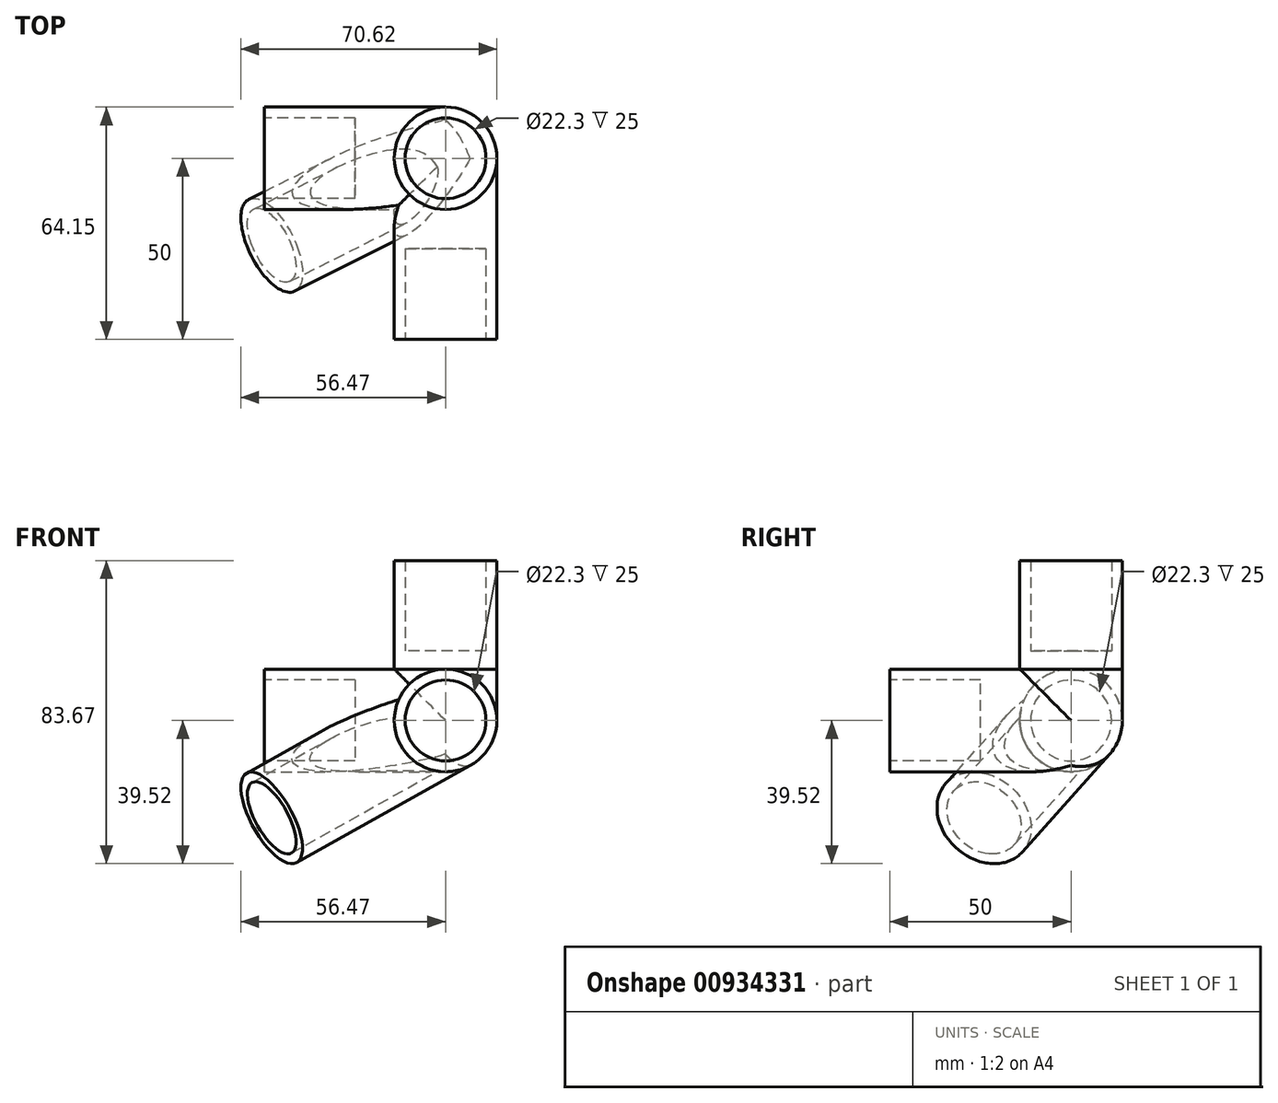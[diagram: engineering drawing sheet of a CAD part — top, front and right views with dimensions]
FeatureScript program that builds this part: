
annotation { "Feature Type Name" : "Feature", "Feature Type Description" : "" }
export const myFeature = defineFeature(function(context is Context, id is Id, definition is map)
    precondition{}
    {
        {
            var Q0;
            Q0=qCreatedBy(makeId("Top.planeOp"),FACE);
            var sketch = newSketch(context, id + "F0", { "sketchPlane" : qUnion([Q0])});
            skCircle(sketch, "E0", {"center": v(0, 0) * mm, "radius": 11.15 * mm});
            skCircle(sketch, "E1", {"center": v(0, 0) * mm, "radius": 14.15 * mm});
            skSolve(sketch);
        }
        {
            var Q0;
            Q0=qSketchRegion(id+"F0",true);
            extrude(context, id + "F1", {"entities" : qUnion([Q0]), "depth" : 25 * mm, "offsetDistance" : 25 * mm});
        }
        {
            var Q0;
            Q0=qCreatedBy(makeId("Top.planeOp"),FACE);
            var sketch = newSketch(context, id + "F2", { "sketchPlane" : qUnion([Q0])});
            skCircle(sketch, "E2", {"center": v(0, 0) * mm, "radius": 14.15 * mm});
            skSolve(sketch);
        }
        {
            var Q0;
            Q0=qSketchRegion(id+"F2",true);
            extrude(context, id + "F3", {"entities" : qUnion([Q0]), "operationType" : NewBodyOperationType.ADD, "oppositeDirection" : true, "depth" : 5 * mm, "offsetDistance" : 25 * mm});
        }
        {
            var Q0;
            Q0=qCreatedBy(makeId("Right.planeOp"),FACE);
            var sketch = newSketch(context, id + "F4", { "sketchPlane" : qUnion([Q0])});
            skLineSegment(sketch, "E3", {"start": v(0, 0) * mm, "end": v(0, -5) * mm, "construction": true});
            skLineSegment(sketch, "E4", {"start": v(0, -5) * mm, "end": v(0, -19.15) * mm, "construction": true});
            skCircle(sketch, "E5", {"center": v(0, -19.15) * mm, "radius": 14.15 * mm});
            skCircle(sketch, "E6", {"center": v(0, -19.15) * mm, "radius": 11.15 * mm});
            skSolve(sketch);
        }
        {
            var Q0;
            Q0=qSketchRegion(id+"F4",true);
            extrude(context, id + "F5", {"entities" : qUnion([Q0]), "operationType" : NewBodyOperationType.ADD, "oppositeDirection" : true, "depth" : 50 * mm, "offsetDistance" : 25 * mm});
        }
        {
            var Q0;
            Q0=qCreatedBy(makeId("Front.planeOp"),FACE);
            var sketch = newSketch(context, id + "F6", { "sketchPlane" : qUnion([Q0])});
            skLineSegment(sketch, "E7", {"start": v(0, 0) * mm, "end": v(0, -5) * mm, "construction": true});
            skLineSegment(sketch, "E8", {"start": v(0, -5) * mm, "end": v(0, -19.15) * mm, "construction": true});
            skCircle(sketch, "E9", {"center": v(0, -19.15) * mm, "radius": 14.15 * mm});
            skCircle(sketch, "E10", {"center": v(0, -19.15) * mm, "radius": 11.15 * mm});
            skSolve(sketch);
        }
        {
            var Q0;
            Q0=qSketchRegion(id+"F6",true);
            extrude(context, id + "F7", {"entities" : qUnion([Q0]), "operationType" : NewBodyOperationType.ADD, "depth" : 50 * mm, "offsetDistance" : 25 * mm});
        }
        {
            var Q0;
            {var subQ0=sQuery(id+"F4.wireOp",EDGE,"E6");var subQ1=sQuery(id+"F4.wireOp",EDGE,"E5");var subQ2=sQuery(id+"F6.wireOp",EDGE,"E10");var subQ3=sQuery(id+"F6.wireOp",EDGE,"E9");var subQ4=makeQuery(id+"F7.opExtrude","CAP_FACE",FACE,{"disambiguationData":[OSD([subQ3,subQ2])],"isStart":true});Q0=makeQuery(id+"F7.boolean.opBoolean","SPLIT",FACE,{"disambiguationData":[TD([makeQuery(id+"F5.opExtrude","SWEPT_FACE",FACE,{"disambiguationData":[OSD([subQ1])]}),makeQuery(id+"F5.opExtrude","CAP_FACE",FACE,{"disambiguationData":[OSD([subQ1,subQ0])],"isStart":true}),makeQuery(id+"F5.opExtrude","SWEPT_FACE",FACE,{"disambiguationData":[OSD([subQ0])]}),makeQuery(id+"F7.opExtrude","SWEPT_FACE",FACE,{"disambiguationData":[OSD([subQ3])]}),subQ4,makeQuery(id+"F7.opExtrude","SWEPT_FACE",FACE,{"disambiguationData":[OSD([subQ2])]})])],"derivedFrom":subQ4});}
            var sketch = newSketch(context, id + "F8", { "sketchPlane" : qUnion([Q0])});
            skArc(sketch, "E11", {"start": v(-14.15, -19.15) * mm, "mid": v(-10, -29.16) * mm, "end": v(0, -33.3) * mm});
            skLineSegment(sketch, "E12", {"start": v(0, -5) * mm, "end": v(-14.15, -5) * mm});
            skLineSegment(sketch, "E13", {"start": v(-14.15, -19.15) * mm, "end": v(-14.15, -5) * mm});
            skLineSegment(sketch, "E14", {"start": v(0, -33.3) * mm, "end": v(0, -5) * mm});
            skSolve(sketch);
        }
        {
            var Q0;
            Q0=qSketchRegion(id+"F8",true);
            var Q1;
            Q1=sQuery(id+"F8.wireOp",EDGE,"E14");
            revolve(context, id + "F9", {"surfaceOperationType" : NewSurfaceOperationType.NEW, "entities" : qUnion([Q0]), "axis" : qUnion([Q1]), "revolveType" : RevolveType.ONE_DIRECTION, "angle" : 360 * degree});
        }
        {
            var Q0;
            Q0=makeQuery(id+"F5.opExtrude","CAP_FACE",FACE,{"disambiguationData":[OSD([sQuery(id+"F4.wireOp",EDGE,"E5"),sQuery(id+"F4.wireOp",EDGE,"E6")])],"isStart":false});
            var sketch = newSketch(context, id + "F10", { "sketchPlane" : qUnion([Q0])});
            skLineSegment(sketch, "E15", {"start": v(0, 0) * mm, "end": v(0, -33.3) * mm, "construction": true});
            skPoint(sketch, "E16.center.orphan", {"position": v(0, -19.15) * mm});
            skCircle(sketch, "E17", {"center": v(0, -19.15) * mm, "radius": 11.15 * mm});
            skSolve(sketch);
        }
        {
            var Q0;
            Q0=makeQuery(id+"F7.opExtrude","CAP_FACE",FACE,{"disambiguationData":[OSD([sQuery(id+"F6.wireOp",EDGE,"E9"),sQuery(id+"F6.wireOp",EDGE,"E10")])],"isStart":false});
            var sketch = newSketch(context, id + "F11", { "sketchPlane" : qUnion([Q0])});
            skCircle(sketch, "E18", {"center": v(0, -19.15) * mm, "radius": 11.15 * mm});
            skSolve(sketch);
        }
        {
            var Q0;
            Q0=qCreatedBy(makeId("Right.planeOp"),FACE);
            var sketch = newSketch(context, id + "F12", { "sketchPlane" : qUnion([Q0])});
            skLineSegment(sketch, "E19", {"start": v(0, 43.35) * mm, "end": v(0, -51.42) * mm, "construction": true});
            skSolve(sketch);
        }
        {
            var Q0;
            Q0=sQuery(id+"F12.wireOp",EDGE,"E19");
            var Q1;
            Q1=qCreatedBy(makeId("Front.planeOp"),FACE);
            cPlane(context, id + "F13", {"entities" : qUnion([Q0, Q1]), "cplaneType" : CPlaneType.LINE_ANGLE, "offset" : 25 * mm, "angle" : 26.6 * degree, "oppositeDirection" : true, "width" : 150 * mm, "height" : 150 * mm});
        }
        {
            var Q0;
            Q0=qCreatedBy(id+"F13.planeOp",FACE);
            var sketch = newSketch(context, id + "F14", { "sketchPlane" : qUnion([Q0])});
            skLineSegment(sketch, "E20", {"start": v(0, 0) * mm, "end": v(0, -19.15) * mm, "construction": true});
            skLineSegment(sketch, "E21", {"start": v(0, -33.3) * mm, "end": v(0, -19.15) * mm, "construction": true});
            skLineSegment(sketch, "E22", {"start": v(0, -19.15) * mm, "end": v(26.82, -32.58) * mm, "construction": true});
            skLineSegment(sketch, "E23", {"start": v(0, -19.15) * mm, "end": v(69.41, -19.15) * mm, "construction": true});
            skSolve(sketch);
        }
        {
            var Q0;
            Q0=sQuery(id+"F14.wireOp",VERTEX,"E22.end");
            var Q1;
            Q1=sQuery(id+"F14.wireOp",EDGE,"E22");
            cPlane(context, id + "F15", {"entities" : qUnion([Q0, Q1]), "cplaneType" : CPlaneType.LINE_POINT, "offset" : 25 * mm, "width" : 150 * mm, "height" : 150 * mm});
        }
        {
            var Q0;
            Q0=qCreatedBy(id+"F15.planeOp",FACE);
            var sketch = newSketch(context, id + "F16", { "sketchPlane" : qUnion([Q0])});
            skCircle(sketch, "E24", {"center": v(-3.75, -16.7) * mm, "radius": 14.15 * mm});
            skCircle(sketch, "E25", {"center": v(-3.75, -16.7) * mm, "radius": 11.15 * mm});
            skSolve(sketch);
        }
        {
            var Q0;
            Q0=qSketchRegion(id+"F16",true);
            extrude(context, id + "F17", {"entities" : qUnion([Q0]), "operationType" : NewBodyOperationType.ADD, "endBound" : BoundingType.SYMMETRIC, "depth" : 60 * mm, "offsetDistance" : 25 * mm});
        }
        {
            var Q0;
            Q0=qSketchRegion(id+"F10",true);
            extrude(context, id + "F18", {"entities" : qUnion([Q0]), "operationType" : NewBodyOperationType.REMOVE, "oppositeDirection" : true, "depth" : 35 * mm, "offsetDistance" : 25 * mm});
        }
        {
            var Q0;
            Q0=qSketchRegion(id+"F11",true);
            extrude(context, id + "F19", {"entities" : qUnion([Q0]), "operationType" : NewBodyOperationType.REMOVE, "oppositeDirection" : true, "depth" : 30 * mm, "offsetDistance" : 25 * mm});
        }
        {
            var Q0;
            Q0=makeQuery(id+"F5.opExtrude","CAP_FACE",FACE,{"disambiguationData":[OSD([sQuery(id+"F4.wireOp",EDGE,"E5"),sQuery(id+"F4.wireOp",EDGE,"E6")])],"isStart":false});
            var sketch = newSketch(context, id + "F20", { "sketchPlane" : qUnion([Q0])});
            skCircle(sketch, "E26", {"center": v(0, -19.15) * mm, "radius": 11.15 * mm});
            skSolve(sketch);
        }
        {
            var Q0;
            Q0=qSketchRegion(id+"F20",true);
            extrude(context, id + "F21", {"entities" : qUnion([Q0]), "operationType" : NewBodyOperationType.ADD, "oppositeDirection" : true, "depth" : 50 * mm, "offsetDistance" : 25 * mm});
        }
        {
            var Q0;
            Q0=makeQuery(id+"F21.boolean.opBoolean","MERGE",FACE,{"derivedFrom":[makeQuery(id+"F5.opExtrude","CAP_FACE",FACE,{"disambiguationData":[OSD([sQuery(id+"F4.wireOp",EDGE,"E5"),sQuery(id+"F4.wireOp",EDGE,"E6")])],"isStart":false}),makeQuery(id+"F21.opExtrude","CAP_FACE",FACE,{"disambiguationData":[OSD([sQuery(id+"F20.wireOp",EDGE,"E26")])],"isStart":true})]});
            var sketch = newSketch(context, id + "F22", { "sketchPlane" : qUnion([Q0])});
            skCircle(sketch, "E27", {"center": v(0, -19.15) * mm, "radius": 11.15 * mm});
            skSolve(sketch);
        }
        {
            var Q0;
            Q0=qSketchRegion(id+"F22",true);
            extrude(context, id + "F23", {"entities" : qUnion([Q0]), "operationType" : NewBodyOperationType.REMOVE, "oppositeDirection" : true, "depth" : 25 * mm, "offsetDistance" : 25 * mm});
        }
        {
            var Q0;
            Q0=makeQuery(id+"F7.opExtrude","CAP_FACE",FACE,{"disambiguationData":[OSD([sQuery(id+"F6.wireOp",EDGE,"E9"),sQuery(id+"F6.wireOp",EDGE,"E10")])],"isStart":false});
            var sketch = newSketch(context, id + "F24", { "sketchPlane" : qUnion([Q0])});
            skCircle(sketch, "E28", {"center": v(0, -19.15) * mm, "radius": 11.15 * mm});
            skSolve(sketch);
        }
        {
            var Q0;
            Q0=qSketchRegion(id+"F24",true);
            extrude(context, id + "F25", {"entities" : qUnion([Q0]), "operationType" : NewBodyOperationType.ADD, "oppositeDirection" : true, "depth" : 50.1 * mm, "offsetDistance" : 25 * mm});
        }
        {
            var Q0;
            Q0=makeQuery(id+"F25.boolean.opBoolean","MERGE",FACE,{"derivedFrom":[makeQuery(id+"F7.opExtrude","CAP_FACE",FACE,{"disambiguationData":[OSD([sQuery(id+"F6.wireOp",EDGE,"E9"),sQuery(id+"F6.wireOp",EDGE,"E10")])],"isStart":false}),makeQuery(id+"F25.opExtrude","CAP_FACE",FACE,{"disambiguationData":[OSD([sQuery(id+"F24.wireOp",EDGE,"E28")])],"isStart":true})]});
            var sketch = newSketch(context, id + "F26", { "sketchPlane" : qUnion([Q0])});
            skCircle(sketch, "E29", {"center": v(0, -19.15) * mm, "radius": 11.15 * mm});
            skSolve(sketch);
        }
        {
            var Q0;
            Q0=qSketchRegion(id+"F26",true);
            extrude(context, id + "F27", {"entities" : qUnion([Q0]), "operationType" : NewBodyOperationType.REMOVE, "oppositeDirection" : true, "depth" : 25 * mm, "offsetDistance" : 25 * mm});
        }
    });
